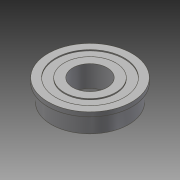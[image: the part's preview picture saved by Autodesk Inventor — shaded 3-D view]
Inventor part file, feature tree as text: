
AUTODESK INVENTOR PART (.ipt)
format: ipt  version: 2014 SP1 (Build 180222100, 222)  size: 96,768 bytes
history: native  units: in
note: dims shown in document units (in); Inventor stores cm internally (conversion verified against a paired STEP export)
features: revolve x1, other x1, imported_body x1
ambient origin geometry x8: Origin, YZ Plane, XZ Plane, XY Plane, X Axis, Y Axis, Z Axis, Center Point
bodies: Body1 (feature_tree)
feature tree (3):
  revolve  "Revolve1"  [1 undecoded]
  other  "217-2731.ipt1"
  imported_body  "Base1"
note: 1 required parameter value undecoded (feature->parameter linkage not recoverable at this tier; creation-order binding heuristic only, values carry confidence <= 0.55)
